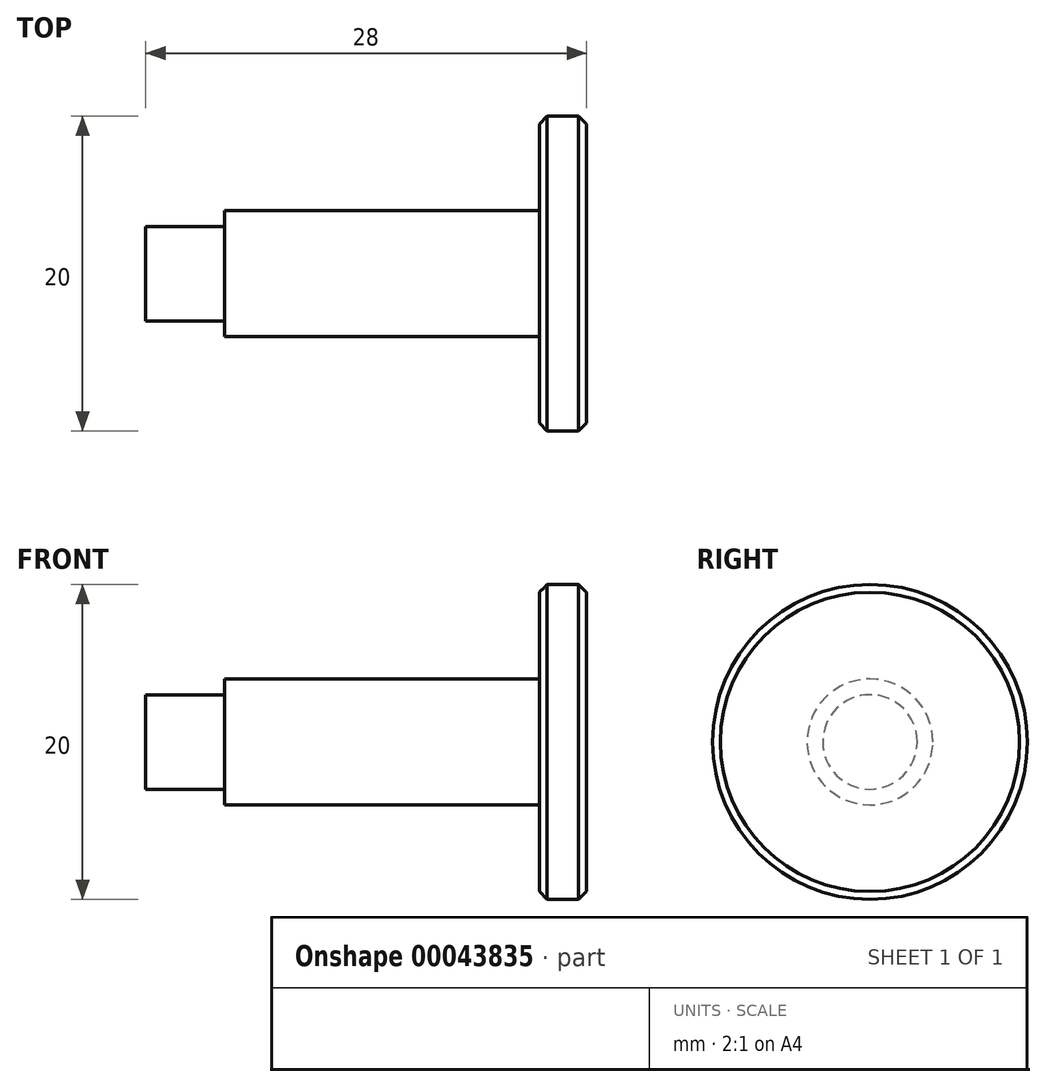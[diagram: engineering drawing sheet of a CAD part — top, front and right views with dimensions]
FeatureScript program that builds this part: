
annotation { "Feature Type Name" : "Feature", "Feature Type Description" : "" }
export const myFeature = defineFeature(function(context is Context, id is Id, definition is map)
    precondition{}
    {
        {
            var Q0;
            Q0=qCreatedBy(makeId("Top.planeOp"),FACE);
            var sketch = newSketch(context, id + "F0", { "sketchPlane" : qUnion([Q0])});
            skLineSegment(sketch, "E0", {"start": v(0, 0) * mm, "end": v(55.96, 0) * mm});
            skLineSegment(sketch, "E1", {"start": v(0, 0) * mm, "end": v(0, 3) * mm});
            skLineSegment(sketch, "E2.0", {"start": v(5, 3) * mm, "end": v(5, 4) * mm});
            skLineSegment(sketch, "E3.0", {"start": v(25, 4) * mm, "end": v(25, 10) * mm});
            skLineSegment(sketch, "E4.0", {"start": v(28, 0) * mm, "end": v(28, 10) * mm});
            skLineSegment(sketch, "E5.0", {"start": v(0, 3) * mm, "end": v(5, 3) * mm});
            skLineSegment(sketch, "E6.0", {"start": v(5, 4) * mm, "end": v(25, 4) * mm});
            skLineSegment(sketch, "E7.0", {"start": v(25, 10) * mm, "end": v(28, 10) * mm});
            skSolve(sketch);
        }
        {
            var Q0;
            Q0 = qSketchRegion(id + "F0", true);
            var Q1;
            Q1=sQuery(id+"F0.wireOp",EDGE,"E0");
            revolve(context, id + "F1", {"entities" : qUnion([Q0]), "axis" : qUnion([Q1]), "revolveType" : RevolveType.FULL});
        }
        {
            var Q0;
            Q0=makeQuery(id+"F1.opRevolve","SWEPT_EDGE",EDGE,{"disambiguationData":[OSD([sQuery(id+"F0.wireOp",EDGE,"E4.0"),sQuery(id+"F0.wireOp",EDGE,"E7.0")])]});
            var Q1;
            Q1=makeQuery(id+"F1.opRevolve","SWEPT_EDGE",EDGE,{"disambiguationData":[OSD([sQuery(id+"F0.wireOp",EDGE,"E3.0"),sQuery(id+"F0.wireOp",EDGE,"E7.0")])]});
            chamfer(context, id + "F2", {"entities" : qUnion([Q0, Q1]), "width" : 0.5 * mm, "tangentPropagation" : true});
        }
    });
